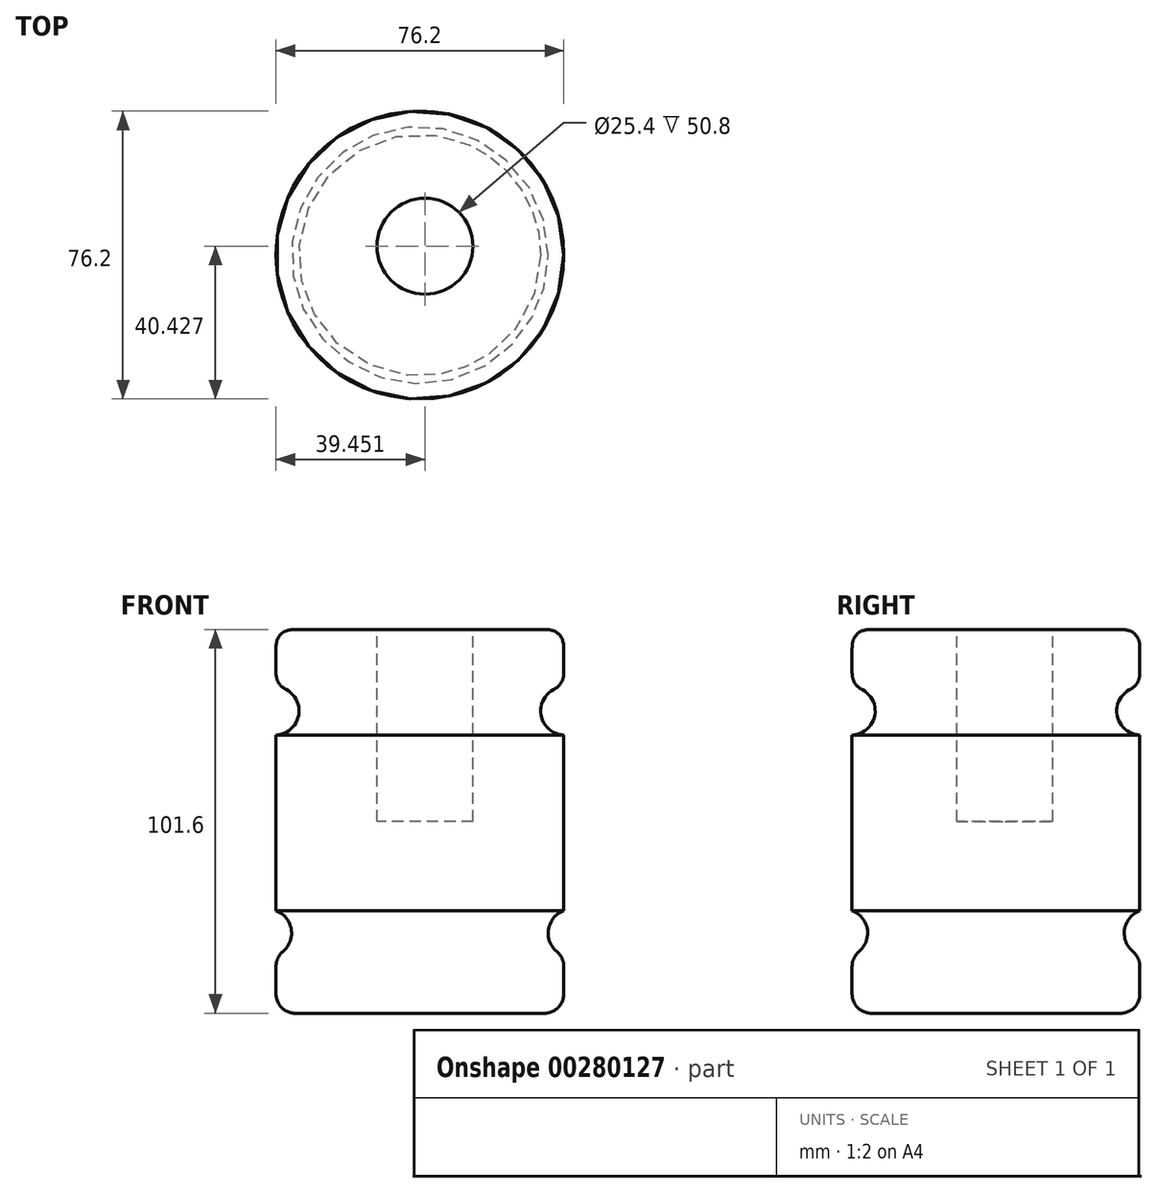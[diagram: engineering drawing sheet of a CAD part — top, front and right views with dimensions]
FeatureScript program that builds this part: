
annotation { "Feature Type Name" : "Feature", "Feature Type Description" : "" }
export const myFeature = defineFeature(function(context is Context, id is Id, definition is map)
    precondition{}
    {
        {
            var Q0;
            Q0=qCreatedBy(makeId("Front.planeOp"),FACE);
            var sketch = newSketch(context, id + "F0", { "sketchPlane" : qUnion([Q0])});
            skLineSegment(sketch, "E0", {"start": v(-25.29, 47.25) * mm, "end": v(12.81, 47.25) * mm});
            skLineSegment(sketch, "E1", {"start": v(12.81, 47.25) * mm, "end": v(12.81, -54.35) * mm});
            skLineSegment(sketch, "E2", {"start": v(12.81, -54.35) * mm, "end": v(-25.29, -54.35) * mm});
            skLineSegment(sketch, "E3", {"start": v(-25.29, -54.35) * mm, "end": v(-25.29, -39.1) * mm});
            skLineSegment(sketch, "E4", {"start": v(-25.29, 47.25) * mm, "end": v(-25.29, 32.01) * mm});
            skArc(sketch, "E5", {"start": v(-25.29, 19.32) * mm, "mid": v(-19.18, 25.67) * mm, "end": v(-25.29, 32.01) * mm});
            skArc(sketch, "E6", {"start": v(-25.29, -39.1) * mm, "mid": v(-21.16, -33.16) * mm, "end": v(-25.29, -27.21) * mm});
            skLineSegment(sketch, "E7", {"start": v(-25.29, -27.21) * mm, "end": v(-25.29, 19.32) * mm});
            skSolve(sketch);
        }
        {
            var Q0;
            Q0=makeQuery(id+"F0.imprint","IMPRINT",FACE,{"disambiguationData":[TD([[makeQuery(id+"F0.imprint","IMPRINT",EDGE,{"derivedFrom":sQuery(id+"F0.wireOp",EDGE,"E0")}),-1.0]])]});
            var Q1;
            Q1=sQuery(id+"F0.wireOp",EDGE,"E1");
            revolve(context, id + "F1", {"entities" : qUnion([Q0]), "axis" : qUnion([Q1]), "revolveType" : RevolveType.FULL});
        }
        {
            var Q0;
            Q0=makeQuery(id+"F1.opRevolve","SWEPT_EDGE",EDGE,{"disambiguationData":[OSD([sQuery(id+"F0.wireOp",EDGE,"E0"),sQuery(id+"F0.wireOp",EDGE,"E4")])]});
            var Q1;
            Q1=makeQuery(id+"F1.opRevolve","SWEPT_FACE",FACE,{"disambiguationData":[OSD([sQuery(id+"F0.wireOp",EDGE,"E4")])]});
            fillet(context, id + "F2", {"entities" : qUnion([Q0, Q1]), "radius" : 5.08 * mm, "rho" : 0.5, "crossSection" : FilletCrossSection.CONIC, "allowEdgeOverflow" : false});
        }
        {
            var Q0;
            Q0=makeQuery(id+"F1.opRevolve","SWEPT_FACE",FACE,{"disambiguationData":[OSD([sQuery(id+"F0.wireOp",EDGE,"E3")])]});
            fillet(context, id + "F3", {"entities" : qUnion([Q0]), "radius" : 5.08 * mm, "tangentPropagation" : true, "allowEdgeOverflow" : false});
        }
        {
            var Q0;
            Q0=makeQuery(id+"F1.opRevolve","SWEPT_FACE",FACE,{"disambiguationData":[OSD([sQuery(id+"F0.wireOp",EDGE,"E0")])]});
            var sketch = newSketch(context, id + "F4", { "sketchPlane" : qUnion([Q0])});
            skCircle(sketch, "E8", {"center": v(14.16, 2.33) * mm, "radius": 12.7 * mm});
            skSolve(sketch);
        }
        {
            var Q0;
            Q0 = qSketchRegion(id + "F4", true);
            extrude(context, id + "F5", {"entities" : qUnion([Q0]), "operationType" : NewBodyOperationType.REMOVE, "oppositeDirection" : true, "depth" : 50.8 * mm});
        }
    });
